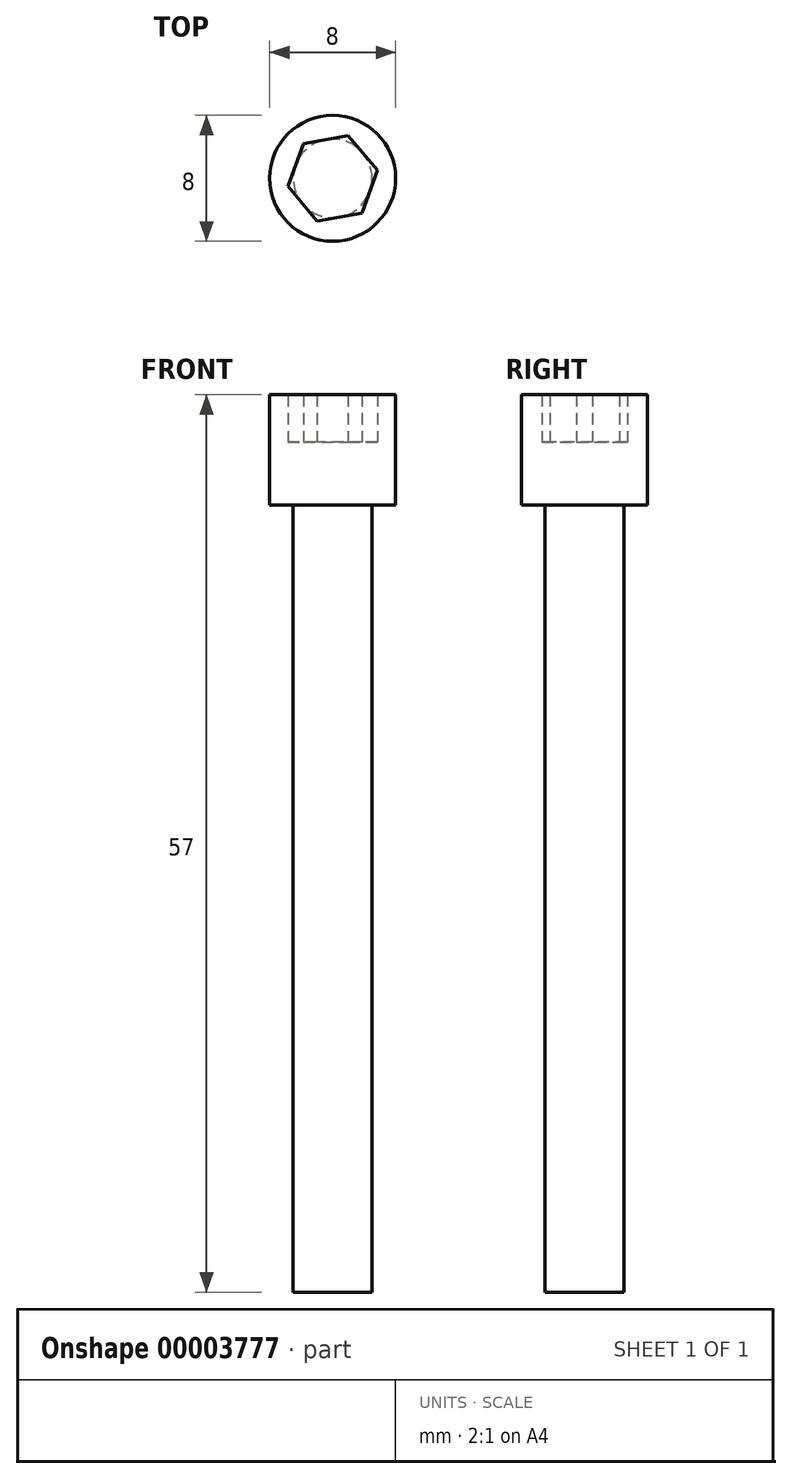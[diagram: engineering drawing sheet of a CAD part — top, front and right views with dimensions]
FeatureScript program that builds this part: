
annotation { "Feature Type Name" : "Feature", "Feature Type Description" : "" }
export const myFeature = defineFeature(function(context is Context, id is Id, definition is map)
    precondition{}
    {
        {
            var Q0;
            Q0=qCreatedBy(makeId("Top.planeOp"),FACE);
            var sketch = newSketch(context, id + "F0", { "sketchPlane" : qUnion([Q0])});
            skCircle(sketch, "E0", {"center": v(0, 0) * mm, "radius": 2.5 * mm});
            skCircle(sketch, "E1.cCircle", {"center": v(0, 0) * mm, "radius": 2.5 * mm, "construction": true});
            skLineSegment(sketch, "E1.0", {"start": v(0.98, 2.72) * mm, "end": v(2.84, 0.51) * mm});
            skLineSegment(sketch, "E1.1", {"start": v(2.84, 0.51) * mm, "end": v(1.86, -2.2) * mm});
            skLineSegment(sketch, "E1.2", {"start": v(1.86, -2.2) * mm, "end": v(-0.98, -2.72) * mm});
            skLineSegment(sketch, "E1.3", {"start": v(-0.98, -2.72) * mm, "end": v(-2.84, -0.51) * mm});
            skLineSegment(sketch, "E1.4", {"start": v(-2.84, -0.51) * mm, "end": v(-1.86, 2.2) * mm});
            skLineSegment(sketch, "E1.5", {"start": v(-1.86, 2.2) * mm, "end": v(0.98, 2.72) * mm});
            skPoint(sketch, "E1.0.midPoint", {"position": v(1.9, 1.61) * mm});
            skCircle(sketch, "E2", {"center": v(0, 0) * mm, "radius": 4 * mm});
            skSolve(sketch);
        }
        {
            var Q0;
            Q0=makeQuery(id+"F0.imprint","IMPRINT",FACE,{"disambiguationData":[TD([[makeQuery(id+"F0.imprint","IMPRINT",EDGE,{"derivedFrom":sQuery(id+"F0.wireOp",EDGE,"E2")}),1.0]])]});
            extrude(context, id + "F8", {"entities" : qUnion([Q0]), "depth" : 3 * mm});
        }
        {
            var Q0;
            {var subQ0=sQuery(id+"F0.wireOp",EDGE,"E0");var subQ6=makeQuery(id+"F0.imprint","INTERSECT",VERTEX,{"derivedFrom":[subQ0,sQuery(id+"F0.wireOp",EDGE,"E1.5")]});Q0=makeQuery(id+"F0.imprint","IMPRINT",FACE,{"disambiguationData":[TD([[makeQuery(id+"F0.imprint","IMPRINT",EDGE,{"disambiguationData":[TD([[subQ6,1.0]])],"derivedFrom":subQ0}),1.0]])]});}
            extrude(context, id + "F9", {"entities" : qUnion([Q0]), "operationType" : NewBodyOperationType.ADD, "oppositeDirection" : true, "depth" : 25 * mm});
        }
        {
            var Q0;
            {var subQ0=sQuery(id+"F0.wireOp",EDGE,"E0");var subQ6=makeQuery(id+"F0.imprint","INTERSECT",VERTEX,{"derivedFrom":[subQ0,sQuery(id+"F0.wireOp",EDGE,"E1.5")]});Q0=makeQuery(id+"F0.imprint","IMPRINT",FACE,{"disambiguationData":[TD([[makeQuery(id+"F0.imprint","IMPRINT",EDGE,{"disambiguationData":[TD([[subQ6,1.0]])],"derivedFrom":subQ0}),1.0]])]});}
            var Q1;
            Q1=makeQuery(id+"F0.imprint","IMPRINT",FACE,{"disambiguationData":[TD([[makeQuery(id+"F0.imprint","IMPRINT",EDGE,{"derivedFrom":sQuery(id+"F0.wireOp",EDGE,"E2")}),1.0]])]});
            var Q2;
            {var subQ1=sQuery(id+"F0.wireOp",EDGE,"E0");var subQ3=sQuery(id+"F0.wireOp",EDGE,"E1.0");var subQ5=makeQuery(id+"F0.imprint","INTERSECT",VERTEX,{"derivedFrom":[subQ1,subQ3]});Q2=makeQuery(id+"F0.imprint","IMPRINT",FACE,{"disambiguationData":[TD([[makeQuery(id+"F0.imprint","IMPRINT",EDGE,{"disambiguationData":[TD([[subQ5,1.0]])],"derivedFrom":subQ1}),-1.0]])]});}
            var Q3;
            {var subQ0=sQuery(id+"F0.wireOp",EDGE,"E1.2");var subQ1=sQuery(id+"F0.wireOp",EDGE,"E0");var subQ2=makeQuery(id+"F0.imprint","INTERSECT",VERTEX,{"derivedFrom":[subQ1,subQ0]});Q3=makeQuery(id+"F0.imprint","IMPRINT",FACE,{"disambiguationData":[TD([[makeQuery(id+"F0.imprint","IMPRINT",EDGE,{"disambiguationData":[TD([[subQ2,-1.0]])],"derivedFrom":subQ1}),-1.0]])]});}
            var Q4;
            {var subQ1=sQuery(id+"F0.wireOp",EDGE,"E0");var subQ3=sQuery(id+"F0.wireOp",EDGE,"E1.3");var subQ5=makeQuery(id+"F0.imprint","INTERSECT",VERTEX,{"derivedFrom":[subQ1,subQ3]});Q4=makeQuery(id+"F0.imprint","IMPRINT",FACE,{"disambiguationData":[TD([[makeQuery(id+"F0.imprint","IMPRINT",EDGE,{"disambiguationData":[TD([[subQ5,-1.0]])],"derivedFrom":subQ1}),-1.0]])]});}
            var Q5;
            {var subQ0=sQuery(id+"F0.wireOp",EDGE,"E1.4");var subQ1=sQuery(id+"F0.wireOp",EDGE,"E0");var subQ2=makeQuery(id+"F0.imprint","INTERSECT",VERTEX,{"derivedFrom":[subQ1,subQ0]});Q5=makeQuery(id+"F0.imprint","IMPRINT",FACE,{"disambiguationData":[TD([[makeQuery(id+"F0.imprint","IMPRINT",EDGE,{"disambiguationData":[TD([[subQ2,-1.0]])],"derivedFrom":subQ1}),-1.0]])]});}
            var Q6;
            {var subQ0=sQuery(id+"F0.wireOp",EDGE,"E1.5");var subQ1=sQuery(id+"F0.wireOp",EDGE,"E0");var subQ2=makeQuery(id+"F0.imprint","INTERSECT",VERTEX,{"derivedFrom":[subQ1,subQ0]});Q6=makeQuery(id+"F0.imprint","IMPRINT",FACE,{"disambiguationData":[TD([[makeQuery(id+"F0.imprint","IMPRINT",EDGE,{"disambiguationData":[TD([[subQ2,1.0]])],"derivedFrom":subQ1}),-1.0]])]});}
            var Q7;
            {var subQ0=sQuery(id+"F0.wireOp",EDGE,"E1.5");var subQ1=sQuery(id+"F0.wireOp",EDGE,"E0");var subQ2=makeQuery(id+"F0.imprint","INTERSECT",VERTEX,{"derivedFrom":[subQ1,subQ0]});Q7=makeQuery(id+"F0.imprint","IMPRINT",FACE,{"disambiguationData":[TD([[makeQuery(id+"F0.imprint","IMPRINT",EDGE,{"disambiguationData":[TD([[subQ2,-1.0]])],"derivedFrom":subQ1}),-1.0]])]});}
            extrude(context, id + "F10", {"entities" : qUnion([Q0, Q1, Q2, Q3, Q4, Q5, Q6, Q7]), "oppositeDirection" : true, "depth" : 2 * mm});
        }
        {
            var Q0;
            {var subQ0=sQuery(id+"F0.wireOp",EDGE,"E0");var subQ6=makeQuery(id+"F0.imprint","INTERSECT",VERTEX,{"derivedFrom":[subQ0,sQuery(id+"F0.wireOp",EDGE,"E1.5")]});Q0=makeQuery(id+"F0.imprint","IMPRINT",FACE,{"disambiguationData":[TD([[makeQuery(id+"F0.imprint","IMPRINT",EDGE,{"disambiguationData":[TD([[subQ6,1.0]])],"derivedFrom":subQ0}),1.0]])]});}
            extrude(context, id + "F11", {"entities" : qUnion([Q0]), "oppositeDirection" : true, "depth" : 52 * mm});
        }
        {
            var Q0;
            {var subQ0=sQuery(id+"F0.wireOp",EDGE,"E1.4");var subQ1=sQuery(id+"F0.wireOp",EDGE,"E0");var subQ2=makeQuery(id+"F0.imprint","INTERSECT",VERTEX,{"derivedFrom":[subQ1,subQ0]});Q0=makeQuery(id+"F0.imprint","IMPRINT",FACE,{"disambiguationData":[TD([[makeQuery(id+"F0.imprint","IMPRINT",EDGE,{"disambiguationData":[TD([[subQ2,-1.0]])],"derivedFrom":subQ1}),-1.0]])]});}
            var Q1;
            {var subQ1=sQuery(id+"F0.wireOp",EDGE,"E0");var subQ3=sQuery(id+"F0.wireOp",EDGE,"E1.3");var subQ5=makeQuery(id+"F0.imprint","INTERSECT",VERTEX,{"derivedFrom":[subQ1,subQ3]});Q1=makeQuery(id+"F0.imprint","IMPRINT",FACE,{"disambiguationData":[TD([[makeQuery(id+"F0.imprint","IMPRINT",EDGE,{"disambiguationData":[TD([[subQ5,-1.0]])],"derivedFrom":subQ1}),-1.0]])]});}
            var Q2;
            {var subQ0=sQuery(id+"F0.wireOp",EDGE,"E1.2");var subQ1=sQuery(id+"F0.wireOp",EDGE,"E0");var subQ2=makeQuery(id+"F0.imprint","INTERSECT",VERTEX,{"derivedFrom":[subQ1,subQ0]});Q2=makeQuery(id+"F0.imprint","IMPRINT",FACE,{"disambiguationData":[TD([[makeQuery(id+"F0.imprint","IMPRINT",EDGE,{"disambiguationData":[TD([[subQ2,-1.0]])],"derivedFrom":subQ1}),-1.0]])]});}
            var Q3;
            {var subQ1=sQuery(id+"F0.wireOp",EDGE,"E0");var subQ3=sQuery(id+"F0.wireOp",EDGE,"E1.0");var subQ5=makeQuery(id+"F0.imprint","INTERSECT",VERTEX,{"derivedFrom":[subQ1,subQ3]});Q3=makeQuery(id+"F0.imprint","IMPRINT",FACE,{"disambiguationData":[TD([[makeQuery(id+"F0.imprint","IMPRINT",EDGE,{"disambiguationData":[TD([[subQ5,1.0]])],"derivedFrom":subQ1}),-1.0]])]});}
            var Q4;
            {var subQ0=sQuery(id+"F0.wireOp",EDGE,"E1.5");var subQ1=sQuery(id+"F0.wireOp",EDGE,"E0");var subQ2=makeQuery(id+"F0.imprint","INTERSECT",VERTEX,{"derivedFrom":[subQ1,subQ0]});Q4=makeQuery(id+"F0.imprint","IMPRINT",FACE,{"disambiguationData":[TD([[makeQuery(id+"F0.imprint","IMPRINT",EDGE,{"disambiguationData":[TD([[subQ2,1.0]])],"derivedFrom":subQ1}),-1.0]])]});}
            var Q5;
            Q5=makeQuery(id+"F0.imprint","IMPRINT",FACE,{"disambiguationData":[TD([[makeQuery(id+"F0.imprint","IMPRINT",EDGE,{"derivedFrom":sQuery(id+"F0.wireOp",EDGE,"E2")}),1.0]])]});
            var Q6;
            {var subQ0=sQuery(id+"F0.wireOp",EDGE,"E1.5");var subQ1=sQuery(id+"F0.wireOp",EDGE,"E0");var subQ2=makeQuery(id+"F0.imprint","INTERSECT",VERTEX,{"derivedFrom":[subQ1,subQ0]});Q6=makeQuery(id+"F0.imprint","IMPRINT",FACE,{"disambiguationData":[TD([[makeQuery(id+"F0.imprint","IMPRINT",EDGE,{"disambiguationData":[TD([[subQ2,-1.0]])],"derivedFrom":subQ1}),-1.0]])]});}
            var Q7;
            {var subQ0=sQuery(id+"F0.wireOp",EDGE,"E0");var subQ6=makeQuery(id+"F0.imprint","INTERSECT",VERTEX,{"derivedFrom":[subQ0,sQuery(id+"F0.wireOp",EDGE,"E1.5")]});Q7=makeQuery(id+"F0.imprint","IMPRINT",FACE,{"disambiguationData":[TD([[makeQuery(id+"F0.imprint","IMPRINT",EDGE,{"disambiguationData":[TD([[subQ6,1.0]])],"derivedFrom":subQ0}),1.0]])]});}
            extrude(context, id + "F12", {"entities" : qUnion([Q0, Q1, Q2, Q3, Q4, Q5, Q6, Q7]), "operationType" : NewBodyOperationType.ADD, "oppositeDirection" : true, "depth" : 2 * mm});
        }
        {
            var Q0;
            Q0=makeQuery(id+"F0.imprint","IMPRINT",FACE,{"disambiguationData":[TD([[makeQuery(id+"F0.imprint","IMPRINT",EDGE,{"derivedFrom":sQuery(id+"F0.wireOp",EDGE,"E2")}),1.0]])]});
            extrude(context, id + "F1", {"entities" : qUnion([Q0]), "operationType" : NewBodyOperationType.ADD, "depth" : 3 * mm});
        }
        {
            var Q0;
            {var subQ0=sQuery(id+"F0.wireOp",EDGE,"E0");var subQ4=makeQuery(id+"F0.imprint","INTERSECT",VERTEX,{"derivedFrom":[subQ0,sQuery(id+"F0.wireOp",EDGE,"E1.5")]});Q0=makeQuery(id+"F0.imprint","IMPRINT",FACE,{"disambiguationData":[TD([[makeQuery(id+"F0.imprint","IMPRINT",EDGE,{"disambiguationData":[TD([[subQ4,1.0]])],"derivedFrom":subQ0}),1.0]])]});}
            extrude(context, id + "F2", {"entities" : qUnion([Q0]), "oppositeDirection" : true, "depth" : 40 * mm});
        }
        {
            var Q0;
            Q0=makeQuery(id+"F0.imprint","IMPRINT",FACE,{"disambiguationData":[TD([[makeQuery(id+"F0.imprint","IMPRINT",EDGE,{"derivedFrom":sQuery(id+"F0.wireOp",EDGE,"E2")}),1.0]])]});
            var Q1;
            {var subQ0=sQuery(id+"F0.wireOp",EDGE,"E0");var subQ4=makeQuery(id+"F0.imprint","INTERSECT",VERTEX,{"derivedFrom":[subQ0,sQuery(id+"F0.wireOp",EDGE,"E1.5")]});Q1=makeQuery(id+"F0.imprint","IMPRINT",FACE,{"disambiguationData":[TD([[makeQuery(id+"F0.imprint","IMPRINT",EDGE,{"disambiguationData":[TD([[subQ4,1.0]])],"derivedFrom":subQ0}),1.0]])]});}
            var Q2;
            {var subQ0=sQuery(id+"F0.wireOp",EDGE,"E1.2");var subQ1=sQuery(id+"F0.wireOp",EDGE,"E0");var subQ2=makeQuery(id+"F0.imprint","INTERSECT",VERTEX,{"derivedFrom":[subQ1,subQ0]});Q2=makeQuery(id+"F0.imprint","IMPRINT",FACE,{"disambiguationData":[TD([[makeQuery(id+"F0.imprint","IMPRINT",EDGE,{"disambiguationData":[TD([[subQ2,-1.0]])],"derivedFrom":subQ1}),-1.0]])]});}
            var Q3;
            {var subQ0=sQuery(id+"F0.wireOp",EDGE,"E1.3");var subQ1=sQuery(id+"F0.wireOp",EDGE,"E0");var subQ2=makeQuery(id+"F0.imprint","INTERSECT",VERTEX,{"derivedFrom":[subQ1,subQ0]});Q3=makeQuery(id+"F0.imprint","IMPRINT",FACE,{"disambiguationData":[TD([[makeQuery(id+"F0.imprint","IMPRINT",EDGE,{"disambiguationData":[TD([[subQ2,-1.0]])],"derivedFrom":subQ1}),-1.0]])]});}
            var Q4;
            {var subQ0=sQuery(id+"F0.wireOp",EDGE,"E1.4");var subQ1=sQuery(id+"F0.wireOp",EDGE,"E0");var subQ2=makeQuery(id+"F0.imprint","INTERSECT",VERTEX,{"derivedFrom":[subQ1,subQ0]});Q4=makeQuery(id+"F0.imprint","IMPRINT",FACE,{"disambiguationData":[TD([[makeQuery(id+"F0.imprint","IMPRINT",EDGE,{"disambiguationData":[TD([[subQ2,-1.0]])],"derivedFrom":subQ1}),-1.0]])]});}
            var Q5;
            {var subQ1=sQuery(id+"F0.wireOp",EDGE,"E0");var subQ3=sQuery(id+"F0.wireOp",EDGE,"E1.5");var subQ5=makeQuery(id+"F0.imprint","INTERSECT",VERTEX,{"derivedFrom":[subQ1,subQ3]});Q5=makeQuery(id+"F0.imprint","IMPRINT",FACE,{"disambiguationData":[TD([[makeQuery(id+"F0.imprint","IMPRINT",EDGE,{"disambiguationData":[TD([[subQ5,-1.0]])],"derivedFrom":subQ1}),-1.0]])]});}
            var Q6;
            {var subQ1=sQuery(id+"F0.wireOp",EDGE,"E0");var subQ3=sQuery(id+"F0.wireOp",EDGE,"E1.5");var subQ5=makeQuery(id+"F0.imprint","INTERSECT",VERTEX,{"derivedFrom":[subQ1,subQ3]});Q6=makeQuery(id+"F0.imprint","IMPRINT",FACE,{"disambiguationData":[TD([[makeQuery(id+"F0.imprint","IMPRINT",EDGE,{"disambiguationData":[TD([[subQ5,1.0]])],"derivedFrom":subQ1}),-1.0]])]});}
            var Q7;
            {var subQ1=sQuery(id+"F0.wireOp",EDGE,"E0");var subQ3=sQuery(id+"F0.wireOp",EDGE,"E1.0");var subQ5=makeQuery(id+"F0.imprint","INTERSECT",VERTEX,{"derivedFrom":[subQ1,subQ3]});Q7=makeQuery(id+"F0.imprint","IMPRINT",FACE,{"disambiguationData":[TD([[makeQuery(id+"F0.imprint","IMPRINT",EDGE,{"disambiguationData":[TD([[subQ5,1.0]])],"derivedFrom":subQ1}),-1.0]])]});}
            extrude(context, id + "F3", {"entities" : qUnion([Q0, Q1, Q2, Q3, Q4, Q5, Q6, Q7]), "operationType" : NewBodyOperationType.ADD, "depth" : 2 * mm});
        }
        {
            var Q0;
            Q0 = qSketchRegion(id + "F0", true);
            extrude(context, id + "F4", {"entities" : qUnion([Q0]), "operationType" : NewBodyOperationType.ADD, "depth" : 5 * mm});
        }
        {
            var Q0;
            {var subQ0=sQuery(id+"F0.wireOp",EDGE,"E0");var subQ4=makeQuery(id+"F0.imprint","INTERSECT",VERTEX,{"derivedFrom":[subQ0,sQuery(id+"F0.wireOp",EDGE,"E1.5")]});Q0=makeQuery(id+"F0.imprint","IMPRINT",FACE,{"disambiguationData":[TD([[makeQuery(id+"F0.imprint","IMPRINT",EDGE,{"disambiguationData":[TD([[subQ4,1.0]])],"derivedFrom":subQ0}),1.0]])]});}
            extrude(context, id + "F5", {"entities" : qUnion([Q0]), "oppositeDirection" : true, "depth" : 30 * mm});
        }
        {
            var Q0;
            {var subQ0=sQuery(id+"F0.wireOp",EDGE,"E0");var subQ4=makeQuery(id+"F0.imprint","INTERSECT",VERTEX,{"derivedFrom":[subQ0,sQuery(id+"F0.wireOp",EDGE,"E1.5")]});Q0=makeQuery(id+"F0.imprint","IMPRINT",FACE,{"disambiguationData":[TD([[makeQuery(id+"F0.imprint","IMPRINT",EDGE,{"disambiguationData":[TD([[subQ4,1.0]])],"derivedFrom":subQ0}),1.0]])]});}
            var Q1;
            {var subQ0=sQuery(id+"F0.wireOp",EDGE,"E1.4");var subQ1=sQuery(id+"F0.wireOp",EDGE,"E0");var subQ2=makeQuery(id+"F0.imprint","INTERSECT",VERTEX,{"derivedFrom":[subQ1,subQ0]});Q1=makeQuery(id+"F0.imprint","IMPRINT",FACE,{"disambiguationData":[TD([[makeQuery(id+"F0.imprint","IMPRINT",EDGE,{"disambiguationData":[TD([[subQ2,-1.0]])],"derivedFrom":subQ1}),-1.0]])]});}
            var Q2;
            {var subQ0=sQuery(id+"F0.wireOp",EDGE,"E1.3");var subQ1=sQuery(id+"F0.wireOp",EDGE,"E0");var subQ2=makeQuery(id+"F0.imprint","INTERSECT",VERTEX,{"derivedFrom":[subQ1,subQ0]});Q2=makeQuery(id+"F0.imprint","IMPRINT",FACE,{"disambiguationData":[TD([[makeQuery(id+"F0.imprint","IMPRINT",EDGE,{"disambiguationData":[TD([[subQ2,-1.0]])],"derivedFrom":subQ1}),-1.0]])]});}
            var Q3;
            {var subQ0=sQuery(id+"F0.wireOp",EDGE,"E1.2");var subQ1=sQuery(id+"F0.wireOp",EDGE,"E0");var subQ2=makeQuery(id+"F0.imprint","INTERSECT",VERTEX,{"derivedFrom":[subQ1,subQ0]});Q3=makeQuery(id+"F0.imprint","IMPRINT",FACE,{"disambiguationData":[TD([[makeQuery(id+"F0.imprint","IMPRINT",EDGE,{"disambiguationData":[TD([[subQ2,-1.0]])],"derivedFrom":subQ1}),-1.0]])]});}
            var Q4;
            {var subQ1=sQuery(id+"F0.wireOp",EDGE,"E0");var subQ3=sQuery(id+"F0.wireOp",EDGE,"E1.0");var subQ5=makeQuery(id+"F0.imprint","INTERSECT",VERTEX,{"derivedFrom":[subQ1,subQ3]});Q4=makeQuery(id+"F0.imprint","IMPRINT",FACE,{"disambiguationData":[TD([[makeQuery(id+"F0.imprint","IMPRINT",EDGE,{"disambiguationData":[TD([[subQ5,1.0]])],"derivedFrom":subQ1}),-1.0]])]});}
            var Q5;
            {var subQ1=sQuery(id+"F0.wireOp",EDGE,"E0");var subQ3=sQuery(id+"F0.wireOp",EDGE,"E1.5");var subQ5=makeQuery(id+"F0.imprint","INTERSECT",VERTEX,{"derivedFrom":[subQ1,subQ3]});Q5=makeQuery(id+"F0.imprint","IMPRINT",FACE,{"disambiguationData":[TD([[makeQuery(id+"F0.imprint","IMPRINT",EDGE,{"disambiguationData":[TD([[subQ5,1.0]])],"derivedFrom":subQ1}),-1.0]])]});}
            var Q6;
            {var subQ1=sQuery(id+"F0.wireOp",EDGE,"E0");var subQ3=sQuery(id+"F0.wireOp",EDGE,"E1.5");var subQ5=makeQuery(id+"F0.imprint","INTERSECT",VERTEX,{"derivedFrom":[subQ1,subQ3]});Q6=makeQuery(id+"F0.imprint","IMPRINT",FACE,{"disambiguationData":[TD([[makeQuery(id+"F0.imprint","IMPRINT",EDGE,{"disambiguationData":[TD([[subQ5,-1.0]])],"derivedFrom":subQ1}),-1.0]])]});}
            var Q7;
            Q7=makeQuery(id+"F0.imprint","IMPRINT",FACE,{"disambiguationData":[TD([[makeQuery(id+"F0.imprint","IMPRINT",EDGE,{"derivedFrom":sQuery(id+"F0.wireOp",EDGE,"E2")}),1.0]])]});
            extrude(context, id + "F6", {"entities" : qUnion([Q0, Q1, Q2, Q3, Q4, Q5, Q6, Q7]), "operationType" : NewBodyOperationType.ADD, "depth" : 2 * mm});
        }
        {
            var Q0;
            Q0=makeQuery(id+"F0.imprint","IMPRINT",FACE,{"disambiguationData":[TD([[makeQuery(id+"F0.imprint","IMPRINT",EDGE,{"derivedFrom":sQuery(id+"F0.wireOp",EDGE,"E2")}),1.0]])]});
            extrude(context, id + "F7", {"entities" : qUnion([Q0]), "operationType" : NewBodyOperationType.ADD, "depth" : 5 * mm});
        }
    });
